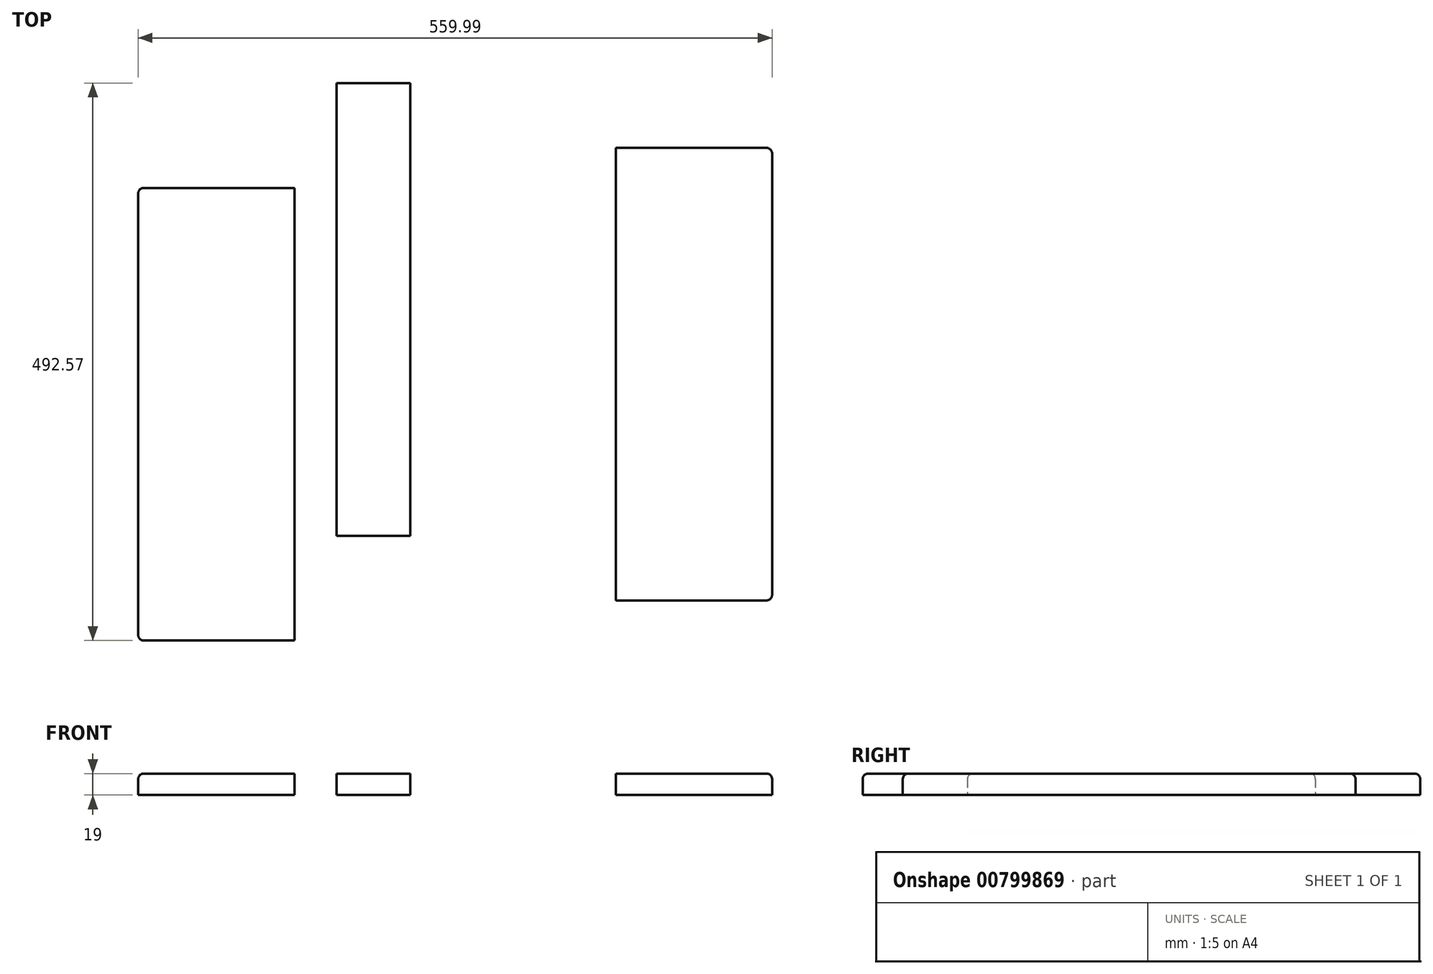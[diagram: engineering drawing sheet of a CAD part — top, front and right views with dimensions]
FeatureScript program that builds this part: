
annotation { "Feature Type Name" : "Feature", "Feature Type Description" : "" }
export const myFeature = defineFeature(function(context is Context, id is Id, definition is map)
    precondition{}
    {
        {
            var Q0;
            Q0=qCreatedBy(makeId("Top.planeOp"),FACE);
            var sketch = newSketch(context, id + "F0", { "sketchPlane" : qUnion([Q0])});
            skLineSegment(sketch, "E0.bottom", {"start": v(-175.37, 279.4) * mm, "end": v(-37.37, 279.4) * mm});
            skLineSegment(sketch, "E0.top", {"start": v(-175.37, -120.6) * mm, "end": v(-37.37, -120.6) * mm});
            skLineSegment(sketch, "E0.left", {"start": v(-175.37, 279.4) * mm, "end": v(-175.37, -120.6) * mm});
            skLineSegment(sketch, "E0.right", {"start": v(-37.37, 279.4) * mm, "end": v(-37.37, -120.6) * mm});
            skSolve(sketch);
        }
        {
            var Q0;
            Q0=qCreatedBy(makeId("Top.planeOp"),FACE);
            var sketch = newSketch(context, id + "F1", { "sketchPlane" : qUnion([Q0])});
            skLineSegment(sketch, "E1.bottom", {"start": v(246.62, 314.86) * mm, "end": v(384.62, 314.86) * mm});
            skLineSegment(sketch, "E1.top", {"start": v(246.62, -85.14) * mm, "end": v(384.62, -85.14) * mm});
            skLineSegment(sketch, "E1.left", {"start": v(246.62, 314.86) * mm, "end": v(246.62, -85.14) * mm});
            skLineSegment(sketch, "E1.right", {"start": v(384.62, 314.86) * mm, "end": v(384.62, -85.14) * mm});
            skSolve(sketch);
        }
        {
            var Q0;
            Q0=qCreatedBy(makeId("Top.planeOp"),FACE);
            var sketch = newSketch(context, id + "F2", { "sketchPlane" : qUnion([Q0])});
            skLineSegment(sketch, "E2.bottom", {"start": v(0, 371.97) * mm, "end": v(65, 371.97) * mm});
            skLineSegment(sketch, "E2.top", {"start": v(0, -28.03) * mm, "end": v(65, -28.03) * mm});
            skLineSegment(sketch, "E2.left", {"start": v(0, 371.97) * mm, "end": v(0, -28.03) * mm});
            skLineSegment(sketch, "E2.right", {"start": v(65, 371.97) * mm, "end": v(65, -28.03) * mm});
            skSolve(sketch);
        }
        {
            var Q0;
            Q0=makeQuery(id+"F0.imprint","IMPRINT",FACE,{"disambiguationData":[TD([[makeQuery(id+"F0.imprint","IMPRINT",EDGE,{"derivedFrom":sQuery(id+"F0.wireOp",EDGE,"E0.bottom")}),-1.0]])]});
            var Q1;
            Q1=makeQuery(id+"F2.imprint","IMPRINT",FACE,{"disambiguationData":[TD([[makeQuery(id+"F2.imprint","IMPRINT",EDGE,{"derivedFrom":sQuery(id+"F2.wireOp",EDGE,"E2.bottom")}),-1.0]])]});
            var Q2;
            Q2=makeQuery(id+"F1.imprint","IMPRINT",FACE,{"disambiguationData":[TD([[makeQuery(id+"F1.imprint","IMPRINT",EDGE,{"derivedFrom":sQuery(id+"F1.wireOp",EDGE,"E1.bottom")}),-1.0]])]});
            extrude(context, id + "F3", {"entities" : qUnion([Q0, Q1, Q2]), "depth" : 19 * mm, "offsetDistance" : 25 * mm});
        }
        {
            var Q0;
            Q0=makeQuery(id+"F3.opExtrude","CAP_EDGE",EDGE,{"disambiguationData":[OSD([sQuery(id+"F0.wireOp",EDGE,"E0.left")])],"isStart":false});
            fillet(context, id + "F4", {"entities" : qUnion([Q0]), "radius" : 5 * mm, "tangentPropagation" : true, "allowEdgeOverflow" : false});
        }
        {
            var Q0;
            Q0=makeQuery(id+"F3.opExtrude","CAP_EDGE",EDGE,{"disambiguationData":[OSD([sQuery(id+"F0.wireOp",EDGE,"E0.top")])],"isStart":false});
            var Q1;
            Q1=makeQuery(id+"F3.opExtrude","CAP_EDGE",EDGE,{"disambiguationData":[OSD([sQuery(id+"F2.wireOp",EDGE,"E2.top")])],"isStart":false});
            fillet(context, id + "F5", {"entities" : qUnion([Q0, Q1]), "radius" : 5 * mm, "tangentPropagation" : true, "allowEdgeOverflow" : false});
        }
        {
            var Q0;
            Q0=makeQuery(id+"F3.opExtrude","CAP_EDGE",EDGE,{"disambiguationData":[OSD([sQuery(id+"F0.wireOp",EDGE,"E0.bottom")])],"isStart":false});
            fillet(context, id + "F6", {"entities" : qUnion([Q0]), "radius" : 5 * mm, "tangentPropagation" : true, "allowEdgeOverflow" : false});
        }
        {
            var Q0;
            Q0=makeQuery(id+"F3.opExtrude","CAP_EDGE",EDGE,{"disambiguationData":[OSD([sQuery(id+"F2.wireOp",EDGE,"E2.bottom")])],"isStart":false});
            fillet(context, id + "F7", {"entities" : qUnion([Q0]), "radius" : 5 * mm, "tangentPropagation" : true, "allowEdgeOverflow" : false});
        }
        {
            var Q0;
            Q0=makeQuery(id+"F3.opExtrude","CAP_EDGE",EDGE,{"disambiguationData":[OSD([sQuery(id+"F1.wireOp",EDGE,"E1.bottom")])],"isStart":false});
            fillet(context, id + "F8", {"entities" : qUnion([Q0]), "radius" : 5 * mm, "tangentPropagation" : true, "allowEdgeOverflow" : false});
        }
        {
            var Q0;
            Q0=makeQuery(id+"F3.opExtrude","CAP_EDGE",EDGE,{"disambiguationData":[OSD([sQuery(id+"F1.wireOp",EDGE,"E1.top")])],"isStart":false});
            fillet(context, id + "F9", {"entities" : qUnion([Q0]), "radius" : 5 * mm, "tangentPropagation" : true, "allowEdgeOverflow" : false});
        }
        {
            var Q0;
            Q0=makeQuery(id+"F3.opExtrude","CAP_EDGE",EDGE,{"disambiguationData":[OSD([sQuery(id+"F1.wireOp",EDGE,"E1.right")])],"isStart":false});
            fillet(context, id + "F10", {"entities" : qUnion([Q0]), "radius" : 5 * mm, "tangentPropagation" : true, "allowEdgeOverflow" : false});
        }
    });
